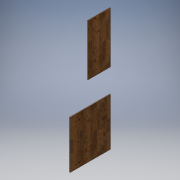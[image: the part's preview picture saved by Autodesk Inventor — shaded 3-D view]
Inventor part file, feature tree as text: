
AUTODESK INVENTOR PART (.ipt)
format: ipt  version: 2016 (Build 200138000, 138)  size: 127,488 bytes
history: native  units: mm
features: extrude x1, sketch x1
ambient origin geometry x8: Origin, YZ Plane, XZ Plane, XY Plane, X Axis, Y Axis, Z Axis, Center Point
bodies: Solid1 (feature_tree)
feature tree (2):
  extrude  "Extrusion1"  Depth=10.0mm
  sketch  "Sketch1"  dims[d0=80.0mm d7=10.0mm d8=0.0mm]
